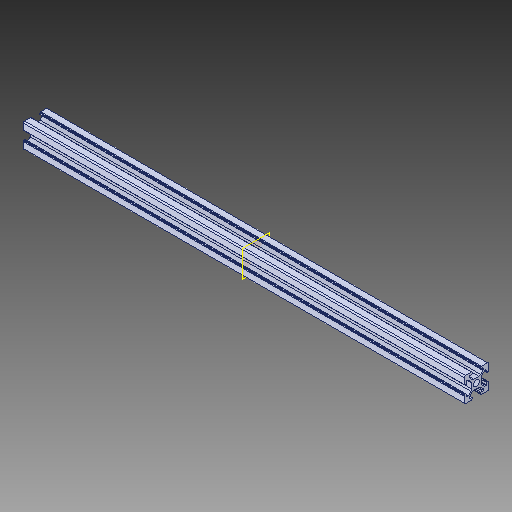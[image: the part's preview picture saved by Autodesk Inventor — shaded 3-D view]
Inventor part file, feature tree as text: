
AUTODESK INVENTOR PART (.ipt)
format: ipt  version: 2018 (Build 220112000, 112)  size: 370,688 bytes
history: native  units: in
note: dims shown in document units (in); Inventor stores cm internally (conversion verified against a paired STEP export)
features: extrude x1, plane x1, sketch x1, projected_geometry x1, fillet x1
ambient origin geometry x8: Origin, YZ Plane, XZ Plane, XY Plane, X Axis, Y Axis, Z Axis, Center Point
bodies: Solid1 (feature_tree)
feature tree (5):
  extrude  "Extrusion2"  [1 undecoded]
  plane  "Work Plane1"
  sketch  "Sketch3"  dims[d2=10.2362in d3=0.0in]
  projected_geometry  "Projected Loop2"
  fillet  "Fillet5"  [1 undecoded]
note: 2 required parameter values undecoded (feature->parameter linkage not recoverable at this tier; creation-order binding heuristic only, values carry confidence <= 0.55)
